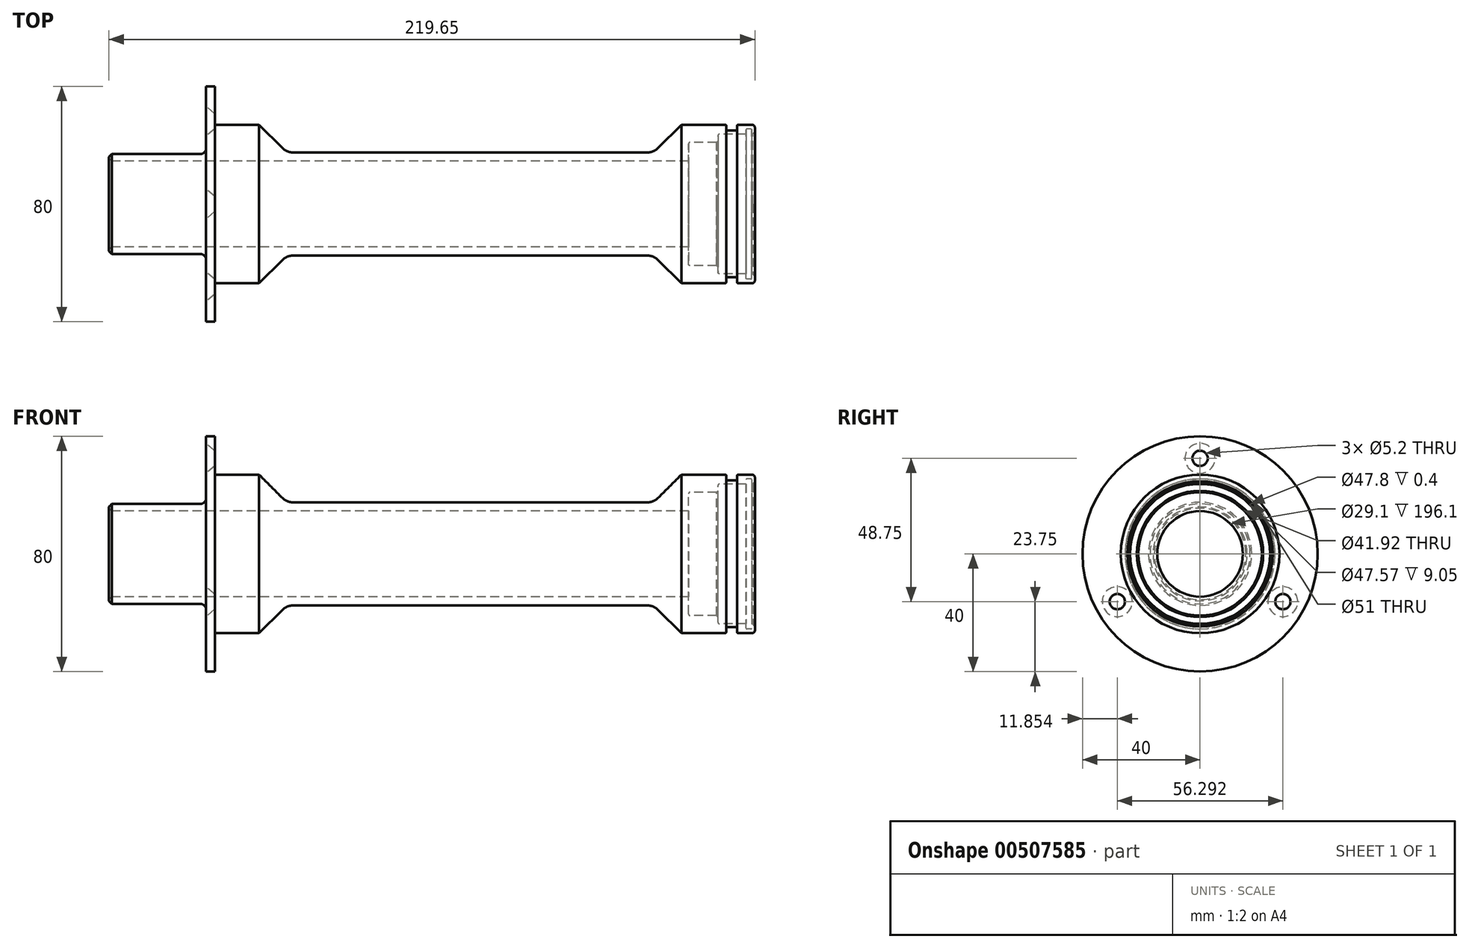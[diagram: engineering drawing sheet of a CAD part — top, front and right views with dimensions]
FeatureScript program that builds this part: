
annotation { "Feature Type Name" : "Feature", "Feature Type Description" : "" }
export const myFeature = defineFeature(function(context is Context, id is Id, definition is map)
    precondition{}
    {
        {
            var Q0;
            Q0=qCreatedBy(makeId("Front.planeOp"),FACE);
            var sketch = newSketch(context, id + "F0", { "sketchPlane" : qUnion([Q0])});
            skLineSegment(sketch, "E0", {"start": v(164.05, 14.55) * mm, "end": v(-33.05, 14.55) * mm});
            skLineSegment(sketch, "E1", {"start": v(-33.05, 14.55) * mm, "end": v(-33.05, 17) * mm});
            skLineSegment(sketch, "E2", {"start": v(-33.05, 17) * mm, "end": v(0, 17) * mm});
            skLineSegment(sketch, "E3", {"start": v(0, 17) * mm, "end": v(0, 22.8) * mm});
            skLineSegment(sketch, "E4", {"start": v(0, 22.8) * mm, "end": v(0, 22.8) * mm});
            skLineSegment(sketch, "E5", {"start": v(0, 22.8) * mm, "end": v(0, 40) * mm});
            skLineSegment(sketch, "E6", {"start": v(0, 40) * mm, "end": v(3, 40) * mm});
            skLineSegment(sketch, "E7", {"start": v(3, 40) * mm, "end": v(3, 26.95) * mm});
            skLineSegment(sketch, "E8", {"start": v(3, 26.95) * mm, "end": v(18, 26.95) * mm});
            skLineSegment(sketch, "E9", {"start": v(186.6, 26.95) * mm, "end": v(186.6, 23.9) * mm});
            skLineSegment(sketch, "E10", {"start": v(186.6, 23.9) * mm, "end": v(185.45, 23.9) * mm});
            skLineSegment(sketch, "E11", {"start": v(185.45, 23.9) * mm, "end": v(185.45, 25.5) * mm});
            skLineSegment(sketch, "E12", {"start": v(185.45, 25.5) * mm, "end": v(183.6, 25.5) * mm});
            skLineSegment(sketch, "E13", {"start": v(183.6, 25.5) * mm, "end": v(183.6, 23.78) * mm});
            skLineSegment(sketch, "E14", {"start": v(183.6, 23.78) * mm, "end": v(174.05, 23.78) * mm});
            skLineSegment(sketch, "E15", {"start": v(174.05, 23.78) * mm, "end": v(174.05, 20.96) * mm});
            skLineSegment(sketch, "E16", {"start": v(174.05, 20.96) * mm, "end": v(164.05, 20.96) * mm});
            skLineSegment(sketch, "E17", {"start": v(164.05, 20.96) * mm, "end": v(164.05, 14.55) * mm});
            skLineSegment(sketch, "E18", {"start": v(0, 0) * mm, "end": v(71.08, 0) * mm});
            skLineSegment(sketch, "E19", {"start": v(27.4, 17.55) * mm, "end": v(152.2, 17.55) * mm});
            skLineSegment(sketch, "E20", {"start": v(161.6, 26.95) * mm, "end": v(152.2, 17.55) * mm});
            skLineSegment(sketch, "E21.trimOffspring", {"start": v(161.6, 26.95) * mm, "end": v(176.8, 26.95) * mm});
            skLineSegment(sketch, "E22", {"start": v(18, 26.95) * mm, "end": v(27.4, 17.55) * mm});
            skLineSegment(sketch, "E23", {"start": v(176.8, 26.95) * mm, "end": v(176.8, 24.95) * mm});
            skLineSegment(sketch, "E24", {"start": v(176.8, 24.95) * mm, "end": v(180.6, 24.95) * mm});
            skLineSegment(sketch, "E25", {"start": v(180.6, 24.95) * mm, "end": v(180.6, 26.95) * mm});
            skLineSegment(sketch, "E26.trimOffspring", {"start": v(180.6, 26.95) * mm, "end": v(186.6, 26.95) * mm});
            skSolve(sketch);
        }
        {
            var Q0;
            Q0=makeQuery(id+"F0.imprint","IMPRINT",FACE,{"disambiguationData":[TD([[makeQuery(id+"F0.imprint","IMPRINT",EDGE,{"derivedFrom":sQuery(id+"F0.wireOp",EDGE,"E0")}),-1.0]])]});
            var Q1;
            Q1=sQuery(id+"F0.wireOp",EDGE,"E18");
            revolve(context, id + "F1", {"entities" : qUnion([Q0]), "axis" : qUnion([Q1]), "revolveType" : RevolveType.FULL});
        }
        {
            var Q0;
            Q0=makeQuery(id+"F1.opRevolve","SWEPT_FACE",FACE,{"disambiguationData":[OSD([sQuery(id+"F0.wireOp",EDGE,"E5")])]});
            var sketch = newSketch(context, id + "F2", { "sketchPlane" : qUnion([Q0])});
            skLineSegment(sketch, "E27", {"start": v(0, 0) * mm, "end": v(0, 32.5) * mm, "construction": true});
            skCircle(sketch, "E28", {"center": v(0, 0) * mm, "radius": 32.5 * mm, "construction": true});
            skLineSegment(sketch, "E29", {"start": v(0, 0) * mm, "end": v(-28.15, -16.25) * mm, "construction": true});
            skLineSegment(sketch, "E30", {"start": v(0, 0) * mm, "end": v(28.15, -16.25) * mm, "construction": true});
            skSolve(sketch);
        }
        {
            var Q0;
            Q0=sQuery(id+"F2.wireOp",VERTEX,"E29.end");
            var Q1;
            Q1=sQuery(id+"F2.wireOp",VERTEX,"E30.end");
            var Q2;
            Q2=sQuery(id+"F2.wireOp",VERTEX,"E27.end");
            var Q3;
            Q3=makeQuery(id+"F1.opRevolve","SWEPT_BODY",BODY,{"disambiguationData":[OSD([sQuery(id+"F0.wireOp",EDGE,"E0"),sQuery(id+"F0.wireOp",EDGE,"E1"),sQuery(id+"F0.wireOp",EDGE,"E2"),sQuery(id+"F0.wireOp",EDGE,"E3"),sQuery(id+"F0.wireOp",EDGE,"E4"),sQuery(id+"F0.wireOp",EDGE,"E5"),sQuery(id+"F0.wireOp",EDGE,"E6"),sQuery(id+"F0.wireOp",EDGE,"E7"),sQuery(id+"F0.wireOp",EDGE,"E8"),sQuery(id+"F0.wireOp",EDGE,"E9"),sQuery(id+"F0.wireOp",EDGE,"E10"),sQuery(id+"F0.wireOp",EDGE,"E11"),sQuery(id+"F0.wireOp",EDGE,"E12"),sQuery(id+"F0.wireOp",EDGE,"E13"),sQuery(id+"F0.wireOp",EDGE,"E14"),sQuery(id+"F0.wireOp",EDGE,"E15"),sQuery(id+"F0.wireOp",EDGE,"E16"),sQuery(id+"F0.wireOp",EDGE,"E17"),sQuery(id+"F0.wireOp",EDGE,"E19"),sQuery(id+"F0.wireOp",EDGE,"E20"),sQuery(id+"F0.wireOp",EDGE,"E21.trimOffspring"),sQuery(id+"F0.wireOp",EDGE,"E22")])]});
            hole(context, id + "F3", {"style" : HoleStyle.C_SINK, "endStyle" : HoleEndStyle.BLIND, "holeDiameter" : 5.2 * mm, "cSinkDiameter" : 10.2 * mm, "cSinkAngle" : 82 * degree, "holeDepth" : 100 * mm, "isTappedThrough" : true, "tappedDepth" : 10.1 * mm, "tapClearance" : 3, "locations" : qUnion([Q0, Q1, Q2]), "scope" : qUnion([Q3])});
        }
        {
            var Q0;
            Q0=makeQuery(id+"F1.opRevolve","SWEPT_EDGE",EDGE,{"disambiguationData":[OSD([sQuery(id+"F0.wireOp",EDGE,"E19"),sQuery(id+"F0.wireOp",EDGE,"E22")])]});
            var Q1;
            Q1=makeQuery(id+"F1.opRevolve","SWEPT_EDGE",EDGE,{"disambiguationData":[OSD([sQuery(id+"F0.wireOp",EDGE,"E19"),sQuery(id+"F0.wireOp",EDGE,"E20")])]});
            fillet(context, id + "F4", {"entities" : qUnion([Q0, Q1]), "radius" : 5 * mm, "tangentPropagation" : true, "allowEdgeOverflow" : false});
        }
        {
            var Q0;
            Q0=makeQuery(id+"F1.opRevolve","SWEPT_EDGE",EDGE,{"disambiguationData":[OSD([sQuery(id+"F0.wireOp",EDGE,"E7"),sQuery(id+"F0.wireOp",EDGE,"E8")])]});
            fillet(context, id + "F5", {"entities" : qUnion([Q0]), "radius" : 0.5 * mm, "tangentPropagation" : true, "allowEdgeOverflow" : false});
        }
        {
            var Q0;
            Q0=makeQuery(id+"F1.opRevolve","SWEPT_EDGE",EDGE,{"disambiguationData":[OSD([sQuery(id+"F0.wireOp",EDGE,"E2"),sQuery(id+"F0.wireOp",EDGE,"E3")])]});
            fillet(context, id + "F6", {"entities" : qUnion([Q0]), "radius" : 2 * mm, "tangentPropagation" : true, "allowEdgeOverflow" : false});
        }
        {
            var Q0;
            Q0=makeQuery(id+"F1.opRevolve","SWEPT_EDGE",EDGE,{"disambiguationData":[OSD([sQuery(id+"F0.wireOp",EDGE,"E1"),sQuery(id+"F0.wireOp",EDGE,"E2")])]});
            var Q1;
            Q1=makeQuery(id+"F1.opRevolve","SWEPT_EDGE",EDGE,{"disambiguationData":[OSD([sQuery(id+"F0.wireOp",EDGE,"E0"),sQuery(id+"F0.wireOp",EDGE,"E1")])]});
            chamfer(context, id + "F7", {"entities" : qUnion([Q0, Q1]), "width" : 1 * mm, "tangentPropagation" : true});
        }
        {
            var Q0;
            Q0=makeQuery(id+"F1.opRevolve","SWEPT_EDGE",EDGE,{"disambiguationData":[OSD([sQuery(id+"F0.wireOp",EDGE,"E9"),sQuery(id+"F0.wireOp",EDGE,"E10")])]});
            chamfer(context, id + "F8", {"entities" : qUnion([Q0]), "width" : 0.75 * mm, "tangentPropagation" : true});
        }
        {
            var Q0;
            Q0=makeQuery(id+"F1.opRevolve","SWEPT_EDGE",EDGE,{"disambiguationData":[OSD([sQuery(id+"F0.wireOp",EDGE,"E12"),sQuery(id+"F0.wireOp",EDGE,"E13")])]});
            var Q1;
            Q1=makeQuery(id+"F1.opRevolve","SWEPT_EDGE",EDGE,{"disambiguationData":[OSD([sQuery(id+"F0.wireOp",EDGE,"E11"),sQuery(id+"F0.wireOp",EDGE,"E12")])]});
            fillet(context, id + "F9", {"entities" : qUnion([Q0, Q1]), "radius" : 0.2 * mm, "tangentPropagation" : true, "allowEdgeOverflow" : false});
        }
        {
            var Q0;
            Q0=makeQuery(id+"F1.opRevolve","SWEPT_EDGE",EDGE,{"disambiguationData":[OSD([sQuery(id+"F0.wireOp",EDGE,"E14"),sQuery(id+"F0.wireOp",EDGE,"E15")])]});
            fillet(context, id + "F10", {"entities" : qUnion([Q0]), "radius" : 0.5 * mm, "tangentPropagation" : true, "allowEdgeOverflow" : false});
        }
        {
            var Q0;
            Q0=makeQuery(id+"F1.opRevolve","SWEPT_EDGE",EDGE,{"disambiguationData":[OSD([sQuery(id+"F0.wireOp",EDGE,"E16"),sQuery(id+"F0.wireOp",EDGE,"E17")])]});
            fillet(context, id + "F11", {"entities" : qUnion([Q0]), "radius" : 0.5 * mm, "tangentPropagation" : true, "allowEdgeOverflow" : false});
        }
        {
            var Q0;
            Q0=makeQuery(id+"F1.opRevolve","SWEPT_EDGE",EDGE,{"disambiguationData":[OSD([sQuery(id+"F0.wireOp",EDGE,"E15"),sQuery(id+"F0.wireOp",EDGE,"E16")])]});
            chamfer(context, id + "F12", {"entities" : qUnion([Q0]), "width" : 0.5 * mm, "tangentPropagation" : true});
        }
        {
            var Q0;
            Q0=makeQuery(id+"F1.opRevolve","SWEPT_EDGE",EDGE,{"disambiguationData":[OSD([sQuery(id+"F0.wireOp",EDGE,"E21.trimOffspring"),sQuery(id+"F0.wireOp",EDGE,"E23")])]});
            var Q1;
            Q1=makeQuery(id+"F1.opRevolve","SWEPT_EDGE",EDGE,{"disambiguationData":[OSD([sQuery(id+"F0.wireOp",EDGE,"E25"),sQuery(id+"F0.wireOp",EDGE,"E26.trimOffspring")])]});
            var Q2;
            {var subQ0=sQuery(id+"F0.wireOp",EDGE,"E9");Q2=makeQuery(id+"FQII4igFNbiRfq2_1.opChamfer","BLEND_EDGE",EDGE,{"blendedFrom":[makeQuery(id+"F1.opRevolve","SWEPT_EDGE",EDGE,{"disambiguationData":[OSD([subQ0,sQuery(id+"F0.wireOp",EDGE,"E26.trimOffspring")])]}),makeQuery(id+"F1.opRevolve","SWEPT_FACE",FACE,{"disambiguationData":[OSD([subQ0])]})],"blendedInto":[makeQuery(id+"F1.opRevolve","SWEPT_FACE",FACE,{"disambiguationData":[OSD([subQ0])]})]});}
            fillet(context, id + "F13", {"entities" : qUnion([Q0, Q1, Q2]), "radius" : 0.25 * mm, "tangentPropagation" : true, "allowEdgeOverflow" : false});
        }
        {
            var Q0;
            Q0=makeQuery(id+"F1.opRevolve","SWEPT_EDGE",EDGE,{"disambiguationData":[OSD([sQuery(id+"F0.wireOp",EDGE,"E23"),sQuery(id+"F0.wireOp",EDGE,"E24")])]});
            var Q1;
            Q1=makeQuery(id+"F1.opRevolve","SWEPT_EDGE",EDGE,{"disambiguationData":[OSD([sQuery(id+"F0.wireOp",EDGE,"E24"),sQuery(id+"F0.wireOp",EDGE,"E25")])]});
            fillet(context, id + "F14", {"entities" : qUnion([Q0, Q1]), "radius" : 0.5 * mm, "tangentPropagation" : true, "allowEdgeOverflow" : false});
        }
        {
            var Q0;
            Q0=makeQuery(id+"F1.opRevolve","SWEPT_EDGE",EDGE,{"disambiguationData":[OSD([sQuery(id+"F0.wireOp",EDGE,"E9"),sQuery(id+"F0.wireOp",EDGE,"E26.trimOffspring")])]});
            fillet(context, id + "F15", {"entities" : qUnion([Q0]), "radius" : 1 * mm, "tangentPropagation" : true, "allowEdgeOverflow" : false});
        }
    });
